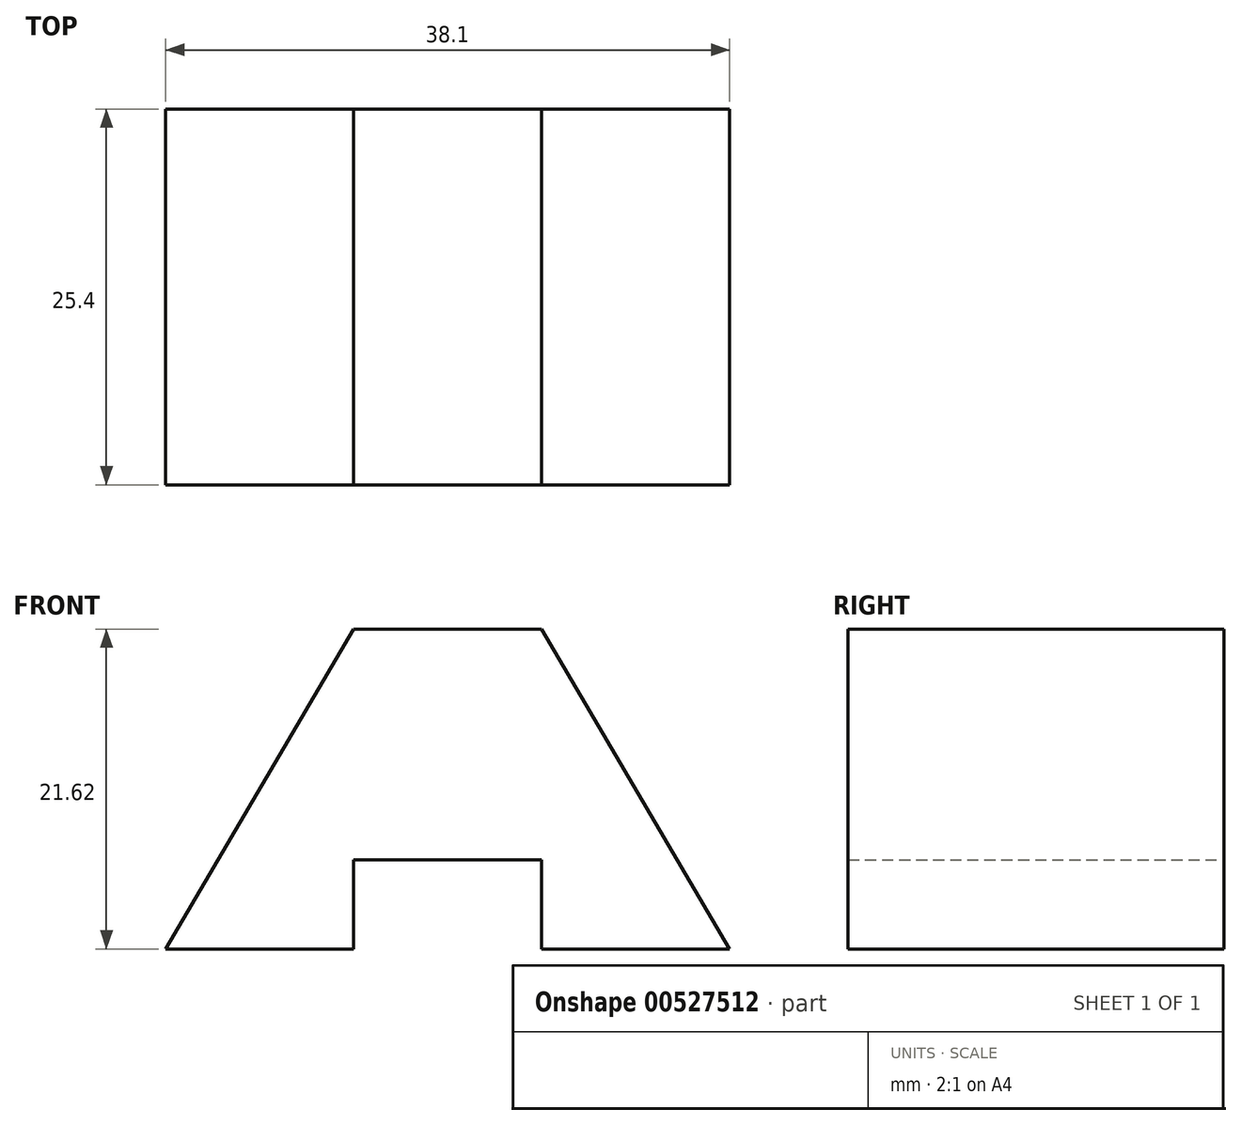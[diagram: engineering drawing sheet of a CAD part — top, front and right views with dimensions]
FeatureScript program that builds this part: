
annotation { "Feature Type Name" : "Feature", "Feature Type Description" : "" }
export const myFeature = defineFeature(function(context is Context, id is Id, definition is map)
    precondition{}
    {
        {
            var Q0;
            Q0=qCreatedBy(makeId("Front.planeOp"),FACE);
            var sketch = newSketch(context, id + "F0", { "sketchPlane" : qUnion([Q0])});
            skLineSegment(sketch, "E0", {"start": v(0, 0) * mm, "end": v(12.7, 0) * mm});
            skLineSegment(sketch, "E1", {"start": v(12.7, 0) * mm, "end": v(12.7, 6) * mm});
            skLineSegment(sketch, "E2", {"start": v(12.7, 6) * mm, "end": v(25.4, 6) * mm});
            skLineSegment(sketch, "E3", {"start": v(25.4, 6) * mm, "end": v(25.4, 0) * mm});
            skLineSegment(sketch, "E4", {"start": v(25.4, 0) * mm, "end": v(38.1, 0) * mm});
            skLineSegment(sketch, "E5", {"start": v(38.1, 0) * mm, "end": v(25.4, 21.62) * mm});
            skLineSegment(sketch, "E6", {"start": v(25.4, 21.62) * mm, "end": v(12.7, 21.62) * mm});
            skLineSegment(sketch, "E7", {"start": v(12.7, 21.62) * mm, "end": v(0, 0) * mm});
            skSolve(sketch);
        }
        {
            var Q0;
            Q0=makeQuery(id+"F0.imprint","IMPRINT",FACE,{"disambiguationData":[TD([[makeQuery(id+"F0.imprint","IMPRINT",EDGE,{"derivedFrom":sQuery(id+"F0.wireOp",EDGE,"E0")}),1.0]])]});
            extrude(context, id + "F1", {"entities" : qUnion([Q0]), "depth" : 25.4 * mm, "offsetDistance" : 25.4 * mm});
        }
    });
